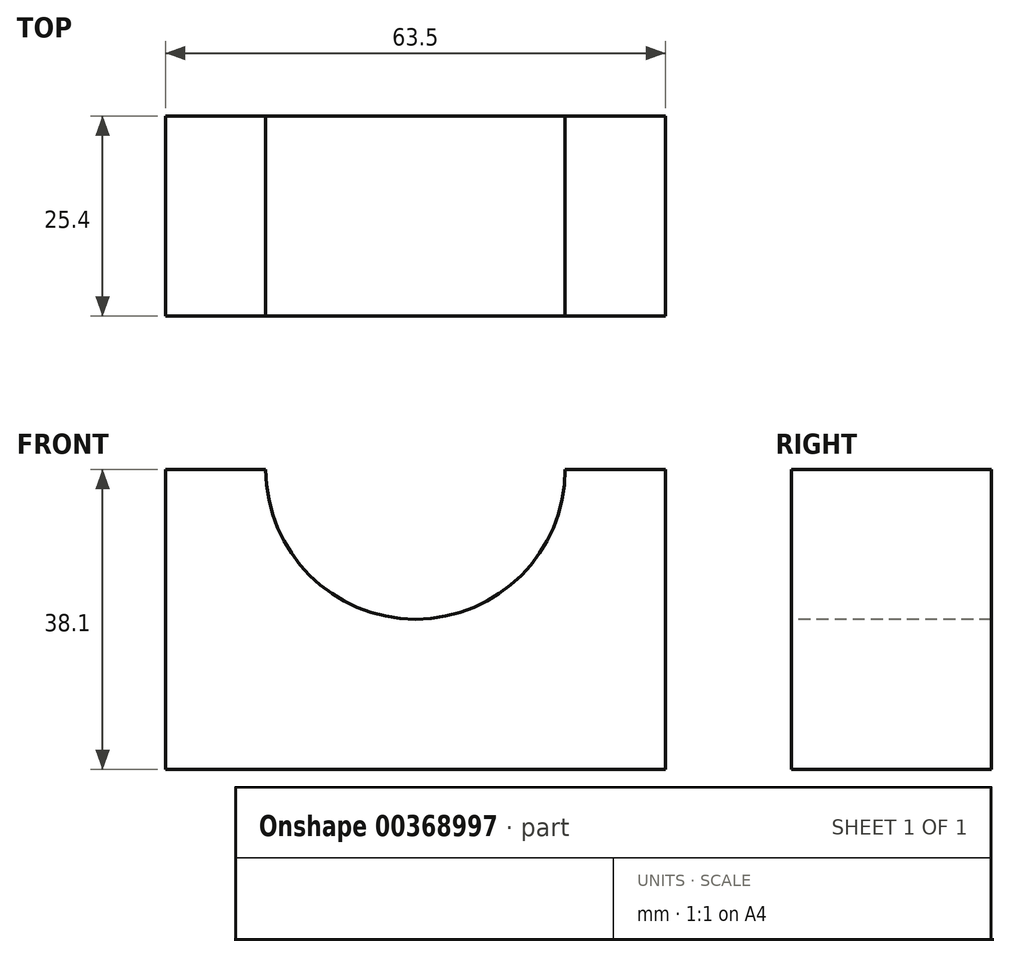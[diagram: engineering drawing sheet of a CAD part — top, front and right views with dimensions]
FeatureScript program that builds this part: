
annotation { "Feature Type Name" : "Feature", "Feature Type Description" : "" }
export const myFeature = defineFeature(function(context is Context, id is Id, definition is map)
    precondition{}
    {
        {
            var Q0;
            Q0=qCreatedBy(makeId("Front.planeOp"),FACE);
            var sketch = newSketch(context, id + "F0", { "sketchPlane" : qUnion([Q0])});
            skLineSegment(sketch, "E0", {"start": v(-50.9, 0) * mm, "end": v(12.6, 0) * mm});
            skLineSegment(sketch, "E1", {"start": v(12.6, 0) * mm, "end": v(12.6, 38.1) * mm});
            skLineSegment(sketch, "E2", {"start": v(12.6, 38.1) * mm, "end": v(-50.9, 38.1) * mm});
            skLineSegment(sketch, "E3", {"start": v(-50.9, 38.1) * mm, "end": v(-50.9, 0) * mm});
            skSolve(sketch);
        }
        {
            var Q0;
            Q0 = qSketchRegion(id + "F0", true);
            extrude(context, id + "F1", {"entities" : qUnion([Q0]), "depth" : 25.4 * mm});
        }
        {
            var Q0;
            Q0=makeQuery(id+"F1.opExtrude","CAP_FACE",FACE,{"disambiguationData":[OSD([sQuery(id+"F0.wireOp",EDGE,"E0"),sQuery(id+"F0.wireOp",EDGE,"E1"),sQuery(id+"F0.wireOp",EDGE,"E2"),sQuery(id+"F0.wireOp",EDGE,"E3")])],"isStart":false});
            var sketch = newSketch(context, id + "F2", { "sketchPlane" : qUnion([Q0])});
            skCircle(sketch, "E4", {"center": v(-19.15, 38.1) * mm, "radius": 19.02 * mm});
            skSolve(sketch);
        }
        {
            var Q0;
            {var subQ0=sQuery(id+"F2.wireOp",EDGE,"E4");var subQ1=makeQuery(id+"F1.opExtrude","CAP_EDGE",EDGE,{"disambiguationData":[OSD([sQuery(id+"F0.wireOp",EDGE,"E2")])],"isStart":false});var subQ2=makeQuery(id+"F2.imprint","INTERSECT",VERTEX,{"disambiguationData":[OD(0.0)],"derivedFrom":[subQ1,subQ0]});Q0=makeQuery(id+"F2.imprint","IMPRINT",FACE,{"disambiguationData":[TD([[makeQuery(id+"F2.imprint","IMPRINT",EDGE,{"disambiguationData":[TD([[subQ2,1.0]])],"derivedFrom":subQ0}),1.0]])]});}
            extrude(context, id + "F3", {"entities" : qUnion([Q0]), "operationType" : NewBodyOperationType.REMOVE, "oppositeDirection" : true, "depth" : 25.4 * mm});
        }
    });
